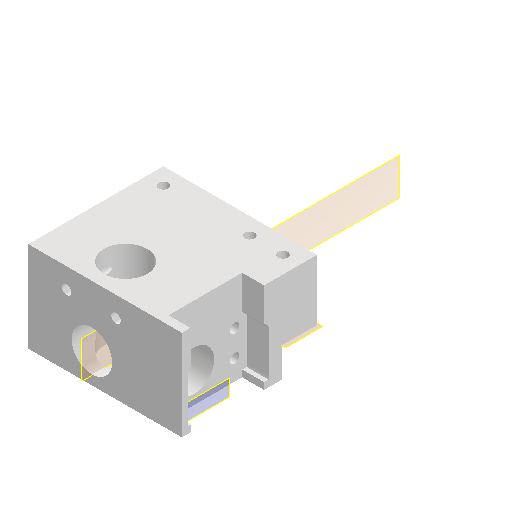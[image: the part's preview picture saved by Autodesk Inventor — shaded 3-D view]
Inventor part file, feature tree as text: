
AUTODESK INVENTOR PART (.ipt)
format: ipt  version: 2025.3 (Build 293356000, 356)  size: 466,944 bytes
history: native  units: mm
features: extrude x17, sketch x15, reference x15, projected_geometry x13, plane x10, other x5
ambient origin geometry x8: Origin, YZ Plane, XZ Plane, XY Plane, X Axis, Y Axis, Z Axis, Center Point
bodies: Volumenkörper2 (feature_tree)
feature tree (75):
  plane  "Arbeitsebene6"
  extrude  "Extrusion12"  Depth=0.5mm
  extrude  "Extrusion13"  Depth=12.0mm
  plane  "Arbeitsebene7"
  plane  "Arbeitsebene8"
  plane  "Arbeitsebene9"
  plane  "Arbeitsebene10"
  sketch  "Skizze21"  dims[d76=35.97mm d77=0.0mm d87=0.5mm]
  plane  "Arbeitsebene11"
  extrude  "Extrusion18"  Depth=0.5mm
  plane  "Arbeitsebene12"
  extrude  "Extrusion22"  TaperAngle=0.0deg  [1 undecoded]
  extrude  "Extrusion23"  Depth=0.5mm
  extrude  "Extrusion27"  TaperAngle=0.0deg  [1 undecoded]
  sketch  "Skizze31"  dims[d107=12.0mm d108=0.0mm d109=0.0mm d110=0.0mm]
  plane  "Arbeitsebene13"
  extrude  "Extrusion28"  Depth=10.0mm
  extrude  "Extrusion29"  Depth=10.0mm TaperAngle=0.0deg
  sketch  "Skizze33"  dims[d111=10.0mm d112=0.0mm d113=0.1mm]
  plane  "Arbeitsebene14"
  extrude  "Extrusion30"  Depth=6.0mm
  sketch  "Skizze35"  dims[d114=0.1mm d116=10.0mm d117=0.0mm]
  plane  "Arbeitsebene15"
  extrude  "Extrusion32"  Depth=2.0mm
  extrude  "Extrusion33"  Depth=2.0mm
  extrude  "Extrusion34"  Depth=10.0mm TaperAngle=0.0deg
  extrude  "Extrusion35"  Depth=8.0mm TaperAngle=0.0deg
  extrude  "Extrusion36"  TaperAngle=0.0deg  [1 undecoded]
  extrude  "Extrusion37"  Depth=2.0mm TaperAngle=0.0deg
  extrude  "Extrusion38"  Depth=10.0mm TaperAngle=0.0deg
  extrude  "Extrusion39"  Depth=10.0mm TaperAngle=0.0deg
  sketch  "Skizze13"  dims[d58=8.0mm d59=0.0mm d60=0.5mm]
  reference  "Referenz11"
  reference  "Referenz12"
  reference  "Referenz13"
  reference  "Referenz14"
  sketch  "Skizze16"  dims[d62=8.0mm d63=0.0mm d75=12.0mm]
  projected_geometry  "Projizierte Kontur9"
  reference  "Referenz15"
  reference  "Referenz25"
  reference  "Referenz26"
  reference  "Referenz27"
  sketch  "Skizze26"  dims[d88=10.0mm d89=0.0mm d90=0.0mm d91=0.0mm]
  sketch  "Skizze30"  dims[d93=20.0mm d94=0.5mm]
  reference  "Referenz30"
  reference  "Referenz31"
  reference  "Referenz32"
  reference  "Referenz33"
  reference  "Referenz34"
  reference  "Referenz35"
  reference  "Referenz36"
  projected_geometry  "Projizierte Kontur16"
  projected_geometry  "Projizierte Kontur17"
  sketch  "Skizze36"  dims[d120=6.0mm d121=9.5mm]
  projected_geometry  "Projizierte Kontur18"
  sketch  "Skizze37"  dims[d122=9.5mm d123=2.0mm]
  projected_geometry  "Projizierte Kontur19"
  projected_geometry  "Projizierte Kontur20"
  sketch  "Skizze38"  dims[d124=2.0mm d125=2.0mm]
  projected_geometry  "Projizierte Kontur21"
  sketch  "Sketch39"  dims[d126=2.5mm d127=10.0mm d128=0.0mm]
  projected_geometry  "Projected Loop22"
  sketch  "Sketch40"  dims[d129=12.0mm d130=8.0mm d131=0.0mm]
  projected_geometry  "Projected Loop23"
  sketch  "Sketch41"  dims[d132=12.8mm d133=0.0mm d134=0.0mm]
  projected_geometry  "Projected Loop24"
  sketch  "Sketch42"  dims[d135=2.8mm d136=8.0mm d137=0.0mm d138=10.0mm d139=0.0mm d140=10.0mm d141=0.0mm d142=2.8mm d143=2.8mm d144=10.0mm d145=0.0mm d146=2.0mm d147=0.0mm d15=0.5mm d16=0.872665mm d17=0.5mm d18=0.872665mm]
  projected_geometry  "Projected Loop25"
  projected_geometry  "Projected Loop26"
  projected_geometry  "Projected Loop27"
  other  "Assemlby_lightsheet_generator_passive_v2.iam"
  other  "30_Scanlens_Laseradaper_lid_v1:1"
  other  "00_SMAConnector_fiber copy:1"
  other  "30_Lightsheet_generator_passive_lid_v1:1"
  other  "30_Laser_to_M12Adapter:1"
note: 3 required parameter values undecoded (feature->parameter linkage not recoverable at this tier; creation-order binding heuristic only, values carry confidence <= 0.55)
